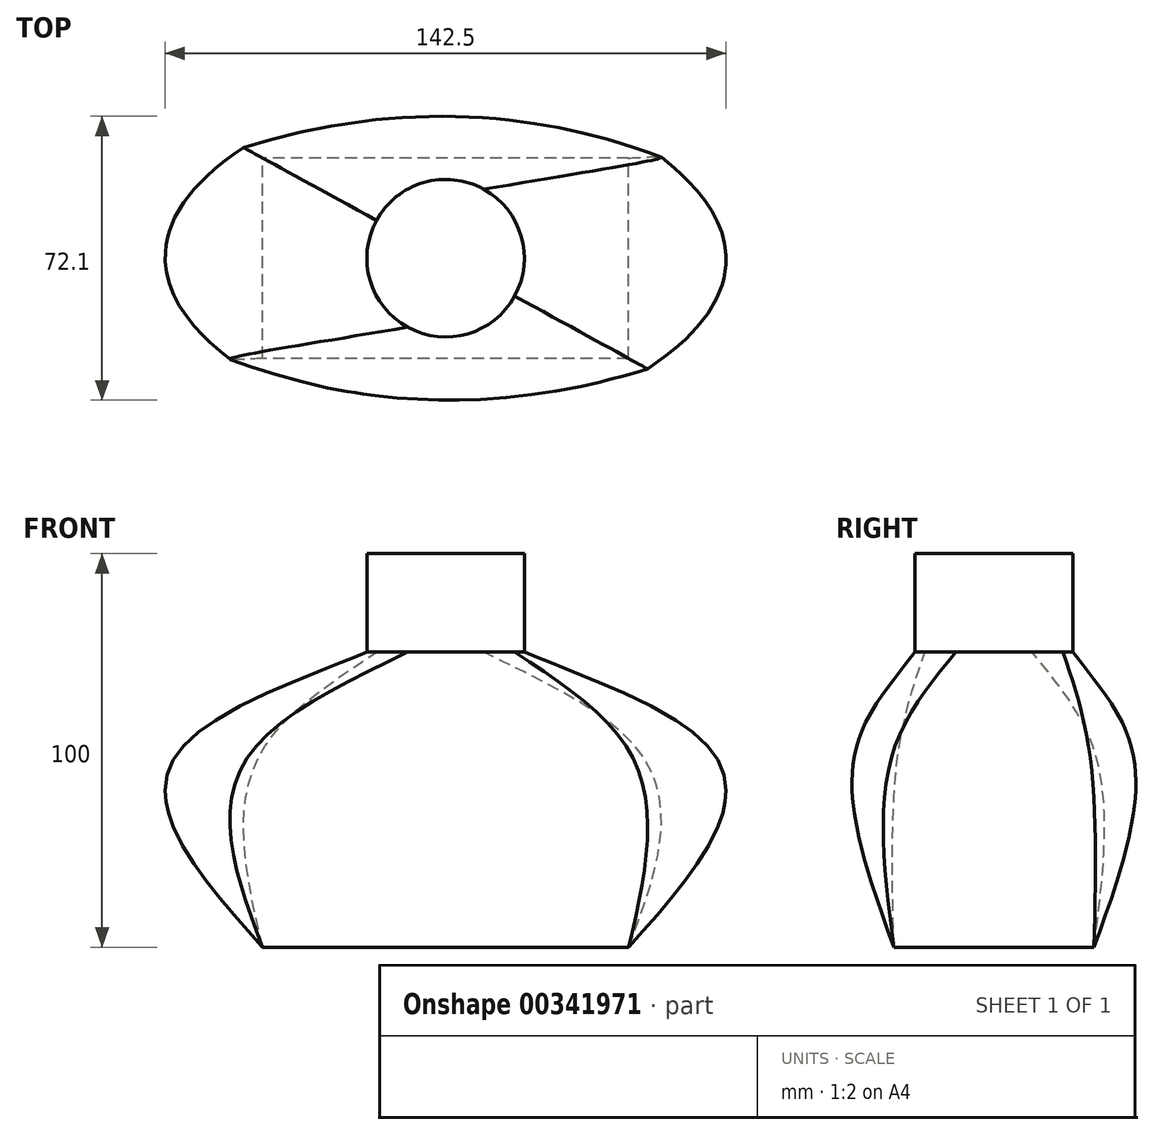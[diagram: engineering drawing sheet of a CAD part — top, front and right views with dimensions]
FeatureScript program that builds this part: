
annotation { "Feature Type Name" : "Feature", "Feature Type Description" : "" }
export const myFeature = defineFeature(function(context is Context, id is Id, definition is map)
    precondition{}
    {
        {
            var Q0;
            Q0=qCreatedBy(makeId("Top.planeOp"),FACE);
            var sketch = newSketch(context, id + "F0", { "sketchPlane" : qUnion([Q0])});
            skLineSegment(sketch, "E0.bottom", {"start": v(46.51, -25.45) * mm, "end": v(-46.51, -25.45) * mm});
            skLineSegment(sketch, "E0.top", {"start": v(46.51, 25.45) * mm, "end": v(-46.51, 25.45) * mm});
            skLineSegment(sketch, "E0.left", {"start": v(46.51, -25.45) * mm, "end": v(46.51, 25.45) * mm});
            skLineSegment(sketch, "E0.right", {"start": v(-46.51, -25.45) * mm, "end": v(-46.51, 25.45) * mm});
            skPoint(sketch, "E0.middle", {"position": v(0, 0) * mm});
            skSolve(sketch);
        }
        {
            var Q0;
            Q0=qCreatedBy(makeId("Top.planeOp"),FACE);
            cPlane(context, id + "F1", {"entities" : qUnion([Q0]), "cplaneType" : CPlaneType.OFFSET, "offset" : 50 * mm, "width" : 150 * mm, "height" : 150 * mm});
        }
        {
            var Q0;
            Q0=qCreatedBy(id+"F1.planeOp",FACE);
            var sketch = newSketch(context, id + "F2", { "sketchPlane" : qUnion([Q0])});
            skEllipse(sketch, "E1", {"center": v(0, 0) * mm, "majorRadius": 67.58 * mm, "minorRadius": 35.15 * mm, "majorAxis": v(-1, 0)});
            skSolve(sketch);
        }
        {
            var Q0;
            Q0=qCreatedBy(id+"F1.planeOp",FACE);
            cPlane(context, id + "F3", {"entities" : qUnion([Q0]), "cplaneType" : CPlaneType.OFFSET, "offset" : 25 * mm, "width" : 150 * mm, "height" : 150 * mm});
        }
        {
            var Q0;
            Q0=qCreatedBy(id+"F3.planeOp",FACE);
            var sketch = newSketch(context, id + "F4", { "sketchPlane" : qUnion([Q0])});
            skCircle(sketch, "E2", {"center": v(0, 0) * mm, "radius": 20.01 * mm});
            skSolve(sketch);
        }
        {
            var Q0;
            Q0=makeQuery(id+"F0.imprint","IMPRINT",FACE,{"disambiguationData":[TD([[makeQuery(id+"F0.imprint","IMPRINT",EDGE,{"derivedFrom":sQuery(id+"F0.wireOp",EDGE,"E0.bottom")}),-1.0]])]});
            var Q1;
            Q1=makeQuery(id+"F2.imprint","IMPRINT",FACE,{"disambiguationData":[TD([[makeQuery(id+"F2.imprint","IMPRINT",EDGE,{"derivedFrom":sQuery(id+"F2.wireOp",EDGE,"E1")}),1.0]])]});
            var Q2;
            Q2=makeQuery(id+"F4.imprint","IMPRINT",FACE,{"disambiguationData":[TD([[makeQuery(id+"F4.imprint","IMPRINT",EDGE,{"derivedFrom":sQuery(id+"F4.wireOp",EDGE,"E2")}),1.0]])]});
            loft(context, id + "F5", {"sheetProfilesArray" : [{ "sheetProfileEntities" : qUnion([Q0]) }, { "sheetProfileEntities" : qUnion([Q1]) }, { "sheetProfileEntities" : qUnion([Q2]) }]});
        }
        {
            var Q0;
            Q0=makeQuery(id+"F5.opLoft","CAP_FACE",FACE,{"disambiguationData":[OSD([makeQuery(id+"F4.imprint","IMPRINT",FACE,{"disambiguationData":[TD([[makeQuery(id+"F4.imprint","IMPRINT",EDGE,{"derivedFrom":sQuery(id+"F4.wireOp",EDGE,"E2")}),1.0]])]})])],"isStart":true});
            extrude(context, id + "F6", {"entities" : qUnion([Q0]), "operationType" : NewBodyOperationType.ADD, "depth" : 25 * mm});
        }
    });
